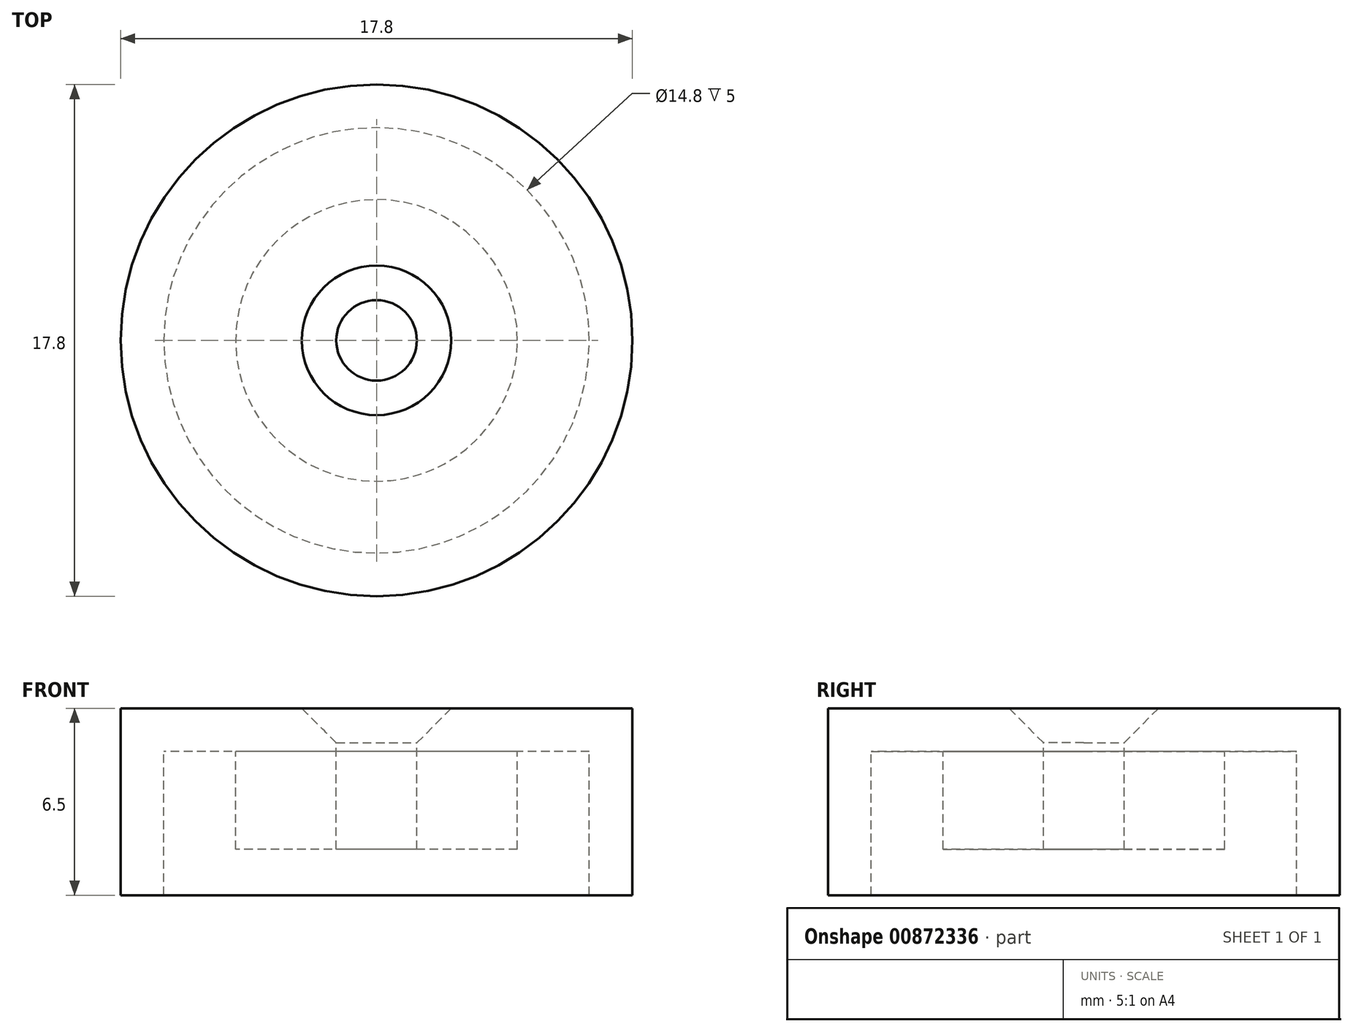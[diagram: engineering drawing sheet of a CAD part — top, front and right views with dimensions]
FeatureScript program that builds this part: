
annotation { "Feature Type Name" : "Feature", "Feature Type Description" : "" }
export const myFeature = defineFeature(function(context is Context, id is Id, definition is map)
    precondition{}
    {
        {
            var Q0;
            Q0=qCreatedBy(makeId("Front.planeOp"),FACE);
            var sketch = newSketch(context, id + "F0", { "sketchPlane" : qUnion([Q0])});
            skLineSegment(sketch, "E0", {"start": v(8.9, 0) * mm, "end": v(8.9, 6.5) * mm});
            skLineSegment(sketch, "E1", {"start": v(8.9, 6.5) * mm, "end": v(0, 6.5) * mm});
            skLineSegment(sketch, "E2", {"start": v(4.9, 1.6) * mm, "end": v(4.9, 5) * mm});
            skLineSegment(sketch, "E3", {"start": v(4.9, 5) * mm, "end": v(7.4, 5) * mm});
            skLineSegment(sketch, "E4", {"start": v(7.4, 5) * mm, "end": v(7.4, 0) * mm});
            skLineSegment(sketch, "E5", {"start": v(0, 1.6) * mm, "end": v(4.9, 1.6) * mm});
            skLineSegment(sketch, "E6", {"start": v(8.9, 0) * mm, "end": v(7.4, 0) * mm});
            skLineSegment(sketch, "E7", {"start": v(1.4, 6.5) * mm, "end": v(1.4, 1.6) * mm});
            skLineSegment(sketch, "E8", {"start": v(0, 15.43) * mm, "end": v(0, -6.74) * mm});
            skSolve(sketch);
        }
        {
            var Q0;
            {var subQ2=sQuery(id+"F0.wireOp",EDGE,"E0");Q0=makeQuery(id+"F0.imprint","IMPRINT",FACE,{"disambiguationData":[TD([[makeQuery(id+"F0.imprint","IMPRINT",EDGE,{"derivedFrom":subQ2}),1.0]])]});}
            var Q1;
            Q1=sQuery(id+"F0.wireOp",EDGE,"E8");
            revolve(context, id + "F1", {"surfaceOperationType" : NewSurfaceOperationType.NEW, "entities" : qUnion([Q0]), "axis" : qUnion([Q1]), "revolveType" : RevolveType.FULL});
        }
        {
            var Q0;
            Q0=makeQuery(id+"F1.opRevolve","SWEPT_EDGE",EDGE,{"disambiguationData":[OSD([sQuery(id+"F0.wireOp",EDGE,"E1"),sQuery(id+"F0.wireOp",EDGE,"E7")])]});
            chamfer(context, id + "F2", {"entities" : qUnion([Q0]), "chamferType" : ChamferType.OFFSET_ANGLE, "width" : 1.2 * mm, "oppositeDirection" : false, "angle" : 45 * degree, "tangentPropagation" : true});
        }
    });
